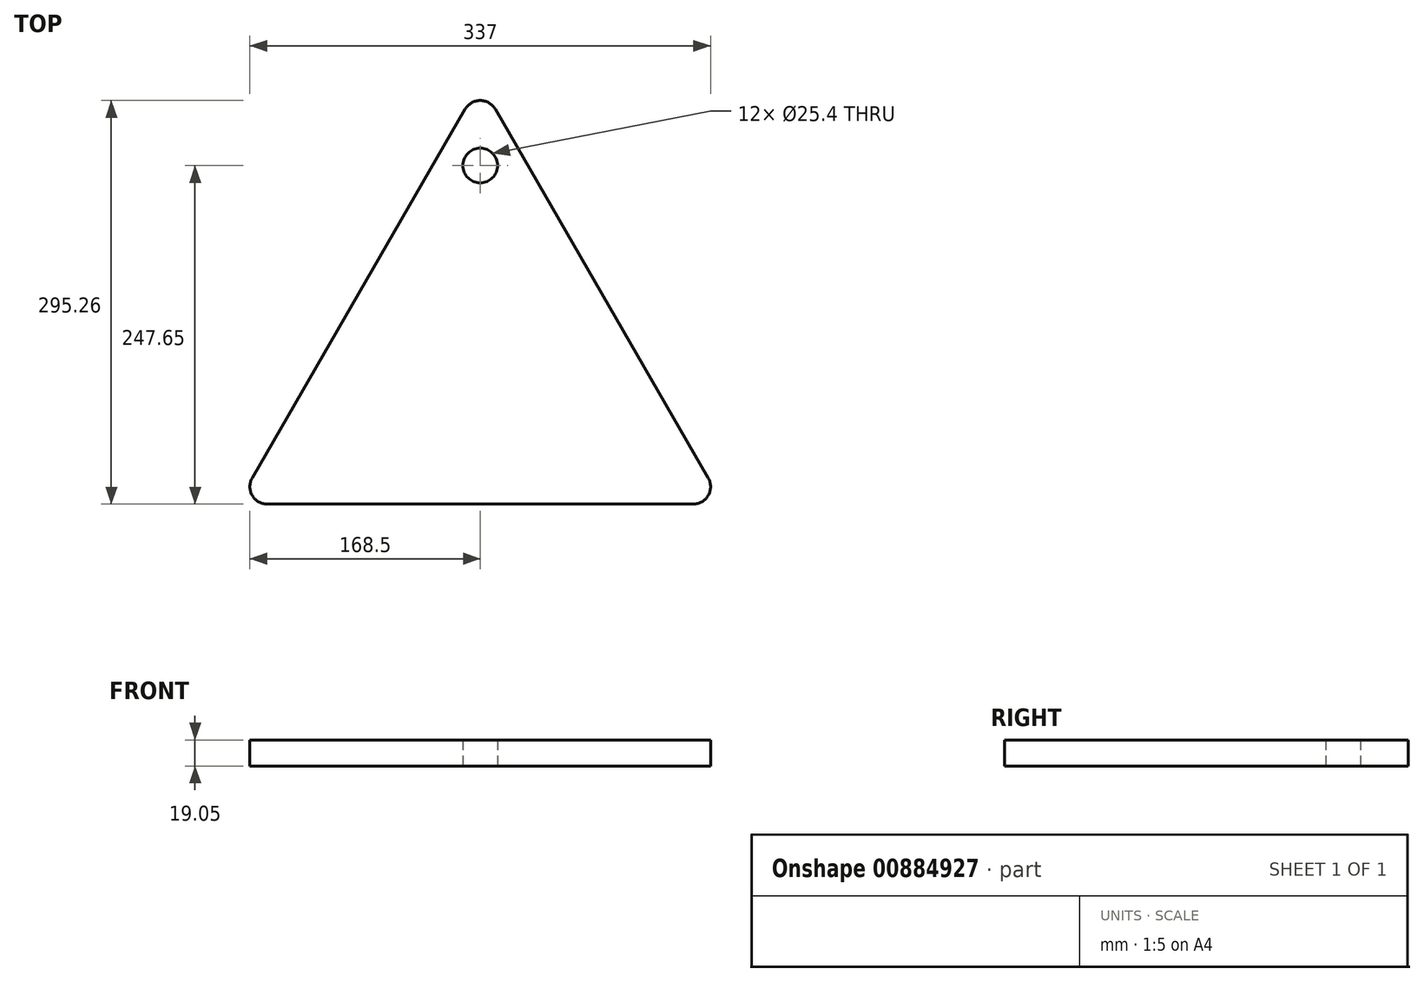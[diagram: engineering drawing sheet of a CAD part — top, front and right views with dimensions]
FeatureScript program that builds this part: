
annotation { "Feature Type Name" : "Feature", "Feature Type Description" : "" }
export const myFeature = defineFeature(function(context is Context, id is Id, definition is map)
    precondition{}
    {
        {
            var Q0;
            Q0=qCreatedBy(makeId("Top.planeOp"),FACE);
            var sketch = newSketch(context, id + "F0", { "sketchPlane" : qUnion([Q0])});
            skLineSegment(sketch, "E0.top", {"start": v(-155.8, -152.4) * mm, "end": v(155.8, -152.4) * mm});
            skLineSegment(sketch, "E1", {"start": v(-11, 136.5) * mm, "end": v(-166.8, -133.35) * mm});
            skLineSegment(sketch, "E2", {"start": v(11, 136.5) * mm, "end": v(166.8, -133.35) * mm});
            skPoint(sketch, "E3.visualSharp", {"position": v(0, 155.56) * mm});
            skArc(sketch, "E3.filletArc", {"start": v(11, 136.5) * mm, "mid": v(0, 142.86) * mm, "end": v(-11, 136.5) * mm});
            skPoint(sketch, "E4.visualSharp", {"position": v(-177.8, -152.4) * mm});
            skArc(sketch, "E4.filletArc", {"start": v(-166.8, -133.35) * mm, "mid": v(-166.8, -146.05) * mm, "end": v(-155.8, -152.4) * mm});
            skPoint(sketch, "E5.visualSharp", {"position": v(177.8, -152.4) * mm});
            skArc(sketch, "E5.filletArc", {"start": v(155.8, -152.4) * mm, "mid": v(166.8, -146.05) * mm, "end": v(166.8, -133.35) * mm});
            skCircle(sketch, "E6", {"center": v(0, 95.25) * mm, "radius": 12.7 * mm});
            skSolve(sketch);
        }
        {
            var Q0;
            Q0 = qSketchRegion(id + "F0", true);
            extrude(context, id + "F1", {"entities" : qUnion([Q0]), "depth" : 19.05 * mm, "offsetDistance" : 25.4 * mm});
        }
    });
